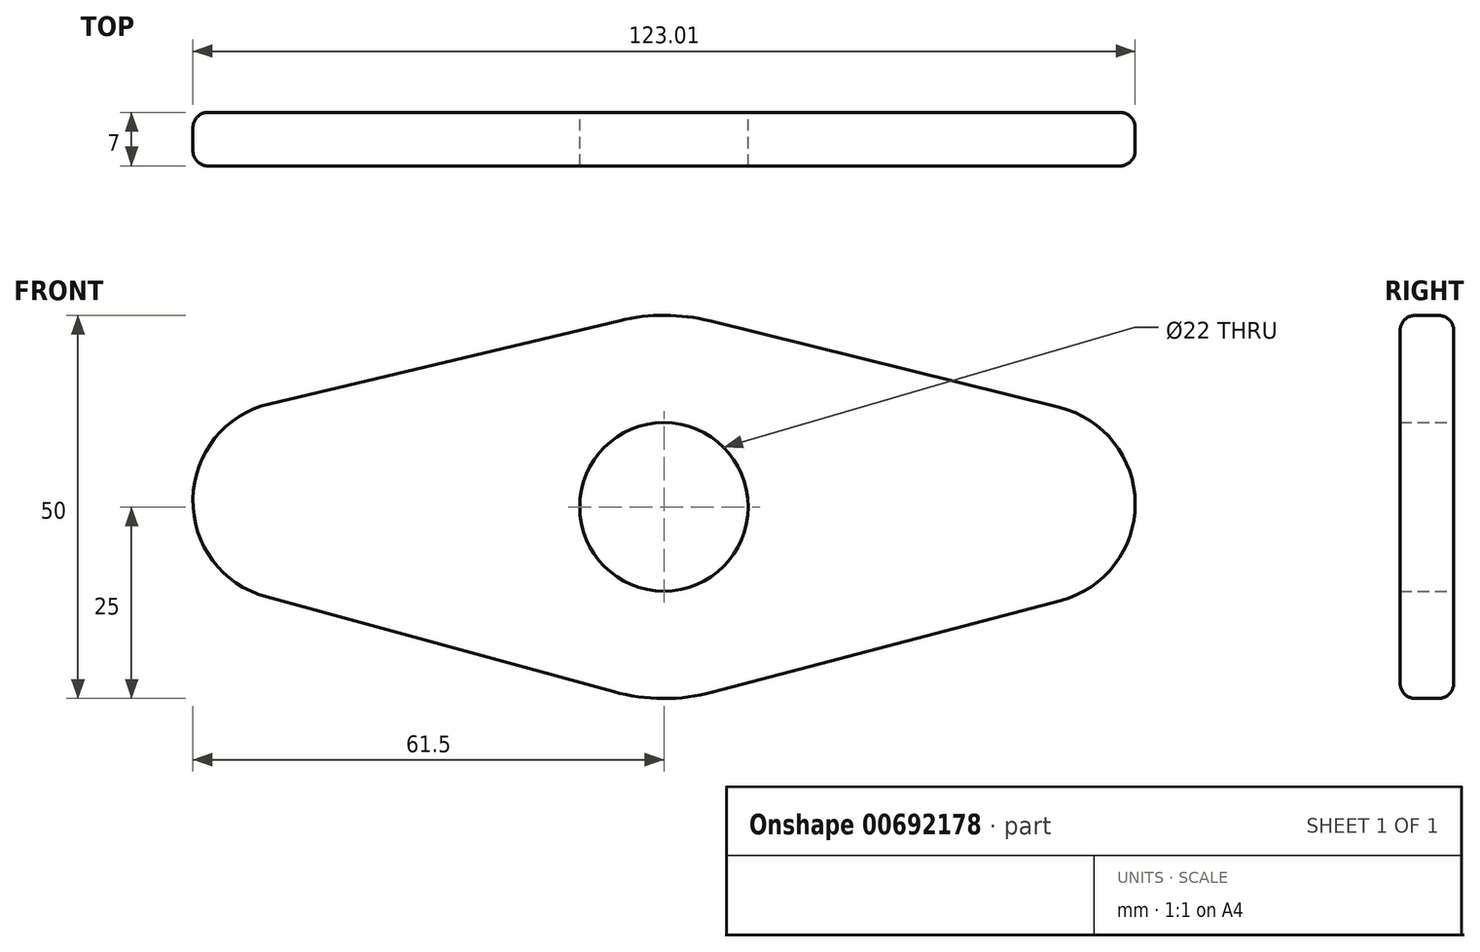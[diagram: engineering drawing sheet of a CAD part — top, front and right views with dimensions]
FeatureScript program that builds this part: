
annotation { "Feature Type Name" : "Feature", "Feature Type Description" : "" }
export const myFeature = defineFeature(function(context is Context, id is Id, definition is map)
    precondition{}
    {
        {
            var Q0;
            Q0=qCreatedBy(makeId("Front.planeOp"),FACE);
            var sketch = newSketch(context, id + "F0", { "sketchPlane" : qUnion([Q0])});
            skCircle(sketch, "E0", {"center": v(0, 0) * mm, "radius": 11 * mm});
            skCircle(sketch, "E1", {"center": v(0, 0) * mm, "radius": 25 * mm});
            skLineSegment(sketch, "E2", {"start": v(-41.96, -10.02) * mm, "end": v(-41.96, -10.02) * mm});
            skCircle(sketch, "E3", {"center": v(48.5, 0.37) * mm, "radius": 13 * mm});
            skCircle(sketch, "E4", {"center": v(-48.5, 0.81) * mm, "radius": 13 * mm});
            skLineSegment(sketch, "E5", {"start": v(-51.5, 13.46) * mm, "end": v(-5.78, 24.32) * mm});
            skLineSegment(sketch, "E6", {"start": v(-51.93, -11.73) * mm, "end": v(-6.59, -24.12) * mm});
            skLineSegment(sketch, "E7", {"start": v(6, 24.27) * mm, "end": v(51.63, 12.99) * mm});
            skLineSegment(sketch, "E8", {"start": v(6.37, -24.18) * mm, "end": v(51.82, -12.2) * mm});
            skSolve(sketch);
        }
        {
            var Q0;
            {var subQ0=sQuery(id+"F0.wireOp",EDGE,"E4");var subQ1=makeQuery(id+"F0.imprint","INTERSECT",VERTEX,{"derivedFrom":[subQ0,sQuery(id+"F0.wireOp",EDGE,"E5")]});Q0=makeQuery(id+"F0.imprint","IMPRINT",FACE,{"disambiguationData":[TD([[makeQuery(id+"F0.imprint","IMPRINT",EDGE,{"disambiguationData":[TD([[subQ1,-1.0]])],"derivedFrom":subQ0}),1.0]])]});}
            var Q1;
            {var subQ0=sQuery(id+"F0.wireOp",EDGE,"E5");Q1=makeQuery(id+"F0.imprint","IMPRINT",FACE,{"disambiguationData":[TD([[makeQuery(id+"F0.imprint","IMPRINT",EDGE,{"derivedFrom":subQ0}),-1.0]])]});}
            var Q2;
            Q2=makeQuery(id+"F0.imprint","IMPRINT",FACE,{"disambiguationData":[TD([[makeQuery(id+"F0.imprint","IMPRINT",EDGE,{"derivedFrom":sQuery(id+"F0.wireOp",EDGE,"E0")}),-1.0]])]});
            var Q3;
            {var subQ0=sQuery(id+"F0.wireOp",EDGE,"E7");Q3=makeQuery(id+"F0.imprint","IMPRINT",FACE,{"disambiguationData":[TD([[makeQuery(id+"F0.imprint","IMPRINT",EDGE,{"derivedFrom":subQ0}),-1.0]])]});}
            var Q4;
            {var subQ0=sQuery(id+"F0.wireOp",EDGE,"E3");var subQ1=makeQuery(id+"F0.imprint","INTERSECT",VERTEX,{"derivedFrom":[subQ0,sQuery(id+"F0.wireOp",EDGE,"E7")]});Q4=makeQuery(id+"F0.imprint","IMPRINT",FACE,{"disambiguationData":[TD([[makeQuery(id+"F0.imprint","IMPRINT",EDGE,{"disambiguationData":[TD([[subQ1,-1.0]])],"derivedFrom":subQ0}),1.0]])]});}
            extrude(context, id + "F1", {"entities" : qUnion([Q0, Q1, Q2, Q3, Q4]), "depth" : 7 * mm, "offsetDistance" : 25 * mm});
        }
        {
            var Q0;
            Q0=makeQuery(id+"F1.opExtrude","CAP_EDGE",EDGE,{"disambiguationData":[OSD([sQuery(id+"F0.wireOp",EDGE,"E5")])],"isStart":false});
            var Q1;
            Q1=makeQuery(id+"F1.opExtrude","CAP_EDGE",EDGE,{"disambiguationData":[OSD([sQuery(id+"F0.wireOp",EDGE,"E7")])],"isStart":true});
            fillet(context, id + "F2", {"entities" : qUnion([Q0, Q1]), "radius" : 2 * mm, "tangentPropagation" : true, "allowEdgeOverflow" : false});
        }
    });
